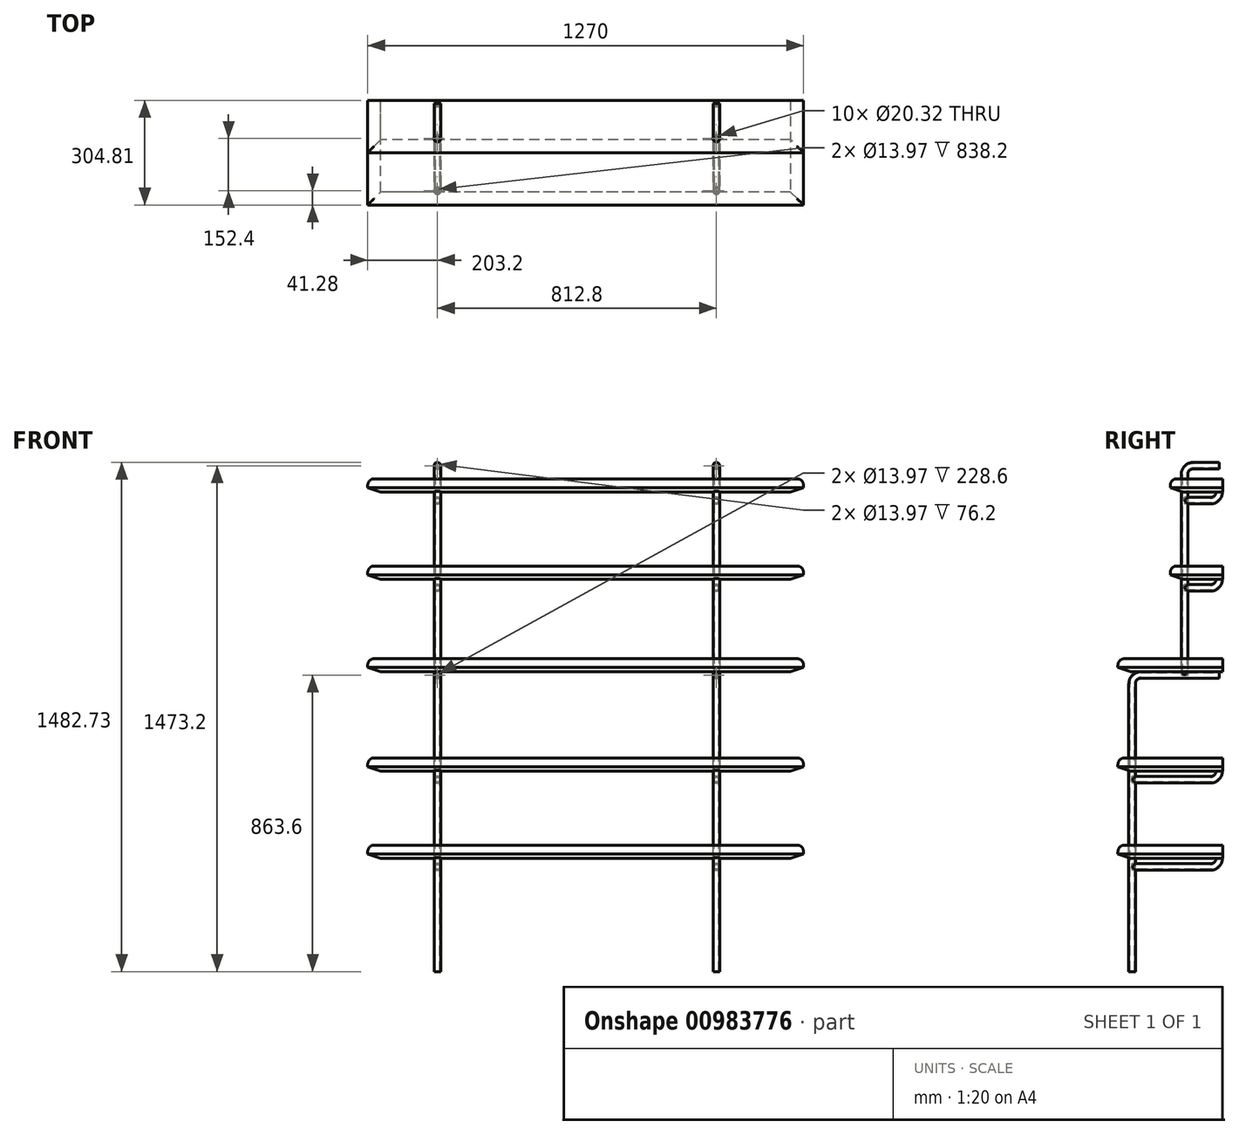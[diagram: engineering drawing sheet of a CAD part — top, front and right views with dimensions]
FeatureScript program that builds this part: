
annotation { "Feature Type Name" : "Feature", "Feature Type Description" : "" }
export const myFeature = defineFeature(function(context is Context, id is Id, definition is map)
    precondition{}
    {
        {
            assignVariable(context, id + "F0", {"name" : "SupportSeparation", "anyValue" : 32});
        }
        {
            var Q0;
            Q0=qCreatedBy(makeId("Right.planeOp"),FACE);
            cPlane(context, id + "F1", {"entities" : qUnion([Q0]), "cplaneType" : CPlaneType.OFFSET, "offset" : (getVariable(context, 'SupportSeparation') / 2) * mm, "width" : 152.4 * mm, "height" : 152.4 * mm});
        }
        {
            var Q0;
            Q0=qCreatedBy(makeId("Top.planeOp"),FACE);
            cPlane(context, id + "F2", {"entities" : qUnion([Q0]), "cplaneType" : CPlaneType.OFFSET, "offset" : 76.2 * mm, "oppositeDirection" : true, "width" : 152.4 * mm, "height" : 152.4 * mm});
        }
        {
            var Q0;
            Q0=qCreatedBy(id+"F1.planeOp",FACE);
            var sketch = newSketch(context, id + "F3", { "sketchPlane" : qUnion([Q0])});
            skLineSegment(sketch, "E0", {"start": v(-127, 0) * mm, "end": v(101.6, 0) * mm});
            skLineSegment(sketch, "E1", {"start": v(0, 0) * mm, "end": v(0, 584.2) * mm});
            skLineSegment(sketch, "E2", {"start": v(25.4, 609.6) * mm, "end": v(101.6, 609.6) * mm});
            skLineSegment(sketch, "E3", {"start": v(-152.4, -25.4) * mm, "end": v(-152.4, -863.6) * mm});
            skLineSegment(sketch, "E4", {"start": v(-152.4, -304.8) * mm, "end": v(76.2, -304.8) * mm});
            skLineSegment(sketch, "E5", {"start": v(-152.4, -558.8) * mm, "end": v(76.2, -558.8) * mm});
            skLineSegment(sketch, "E6", {"start": v(0, 508) * mm, "end": v(76.2, 508) * mm});
            skLineSegment(sketch, "E7", {"start": v(0, 254) * mm, "end": v(76.2, 254) * mm});
            skPoint(sketch, "E8.visualSharp", {"position": v(-152.4, 0) * mm});
            skArc(sketch, "E8.filletArc", {"start": v(-127, 0) * mm, "mid": v(-144.96, -7.44) * mm, "end": v(-152.4, -25.4) * mm});
            skPoint(sketch, "E9.visualSharp", {"position": v(0, 609.6) * mm});
            skArc(sketch, "E9.filletArc", {"start": v(25.4, 609.6) * mm, "mid": v(7.44, 602.16) * mm, "end": v(0, 584.2) * mm});
            skPoint(sketch, "E10.visualSharp", {"position": v(101.6, 508) * mm});
            skArc(sketch, "E10.filletArc", {"start": v(76.2, 508) * mm, "mid": v(94.16, 515.44) * mm, "end": v(101.6, 533.4) * mm});
            skPoint(sketch, "E11.visualSharp", {"position": v(101.6, 254) * mm});
            skArc(sketch, "E11.filletArc", {"start": v(76.2, 254) * mm, "mid": v(94.16, 261.44) * mm, "end": v(101.6, 279.4) * mm});
            skPoint(sketch, "E12.visualSharp", {"position": v(101.6, -304.8) * mm});
            skArc(sketch, "E12.filletArc", {"start": v(76.2, -304.8) * mm, "mid": v(94.16, -297.36) * mm, "end": v(101.6, -279.4) * mm});
            skPoint(sketch, "E13.visualSharp", {"position": v(101.6, -558.8) * mm});
            skArc(sketch, "E13.filletArc", {"start": v(76.2, -558.8) * mm, "mid": v(94.16, -551.36) * mm, "end": v(101.6, -533.4) * mm});
            skSolve(sketch);
        }
        {
            var Q0;
            Q0=qCreatedBy(id+"F2.planeOp",FACE);
            var sketch = newSketch(context, id + "F4", { "sketchPlane" : qUnion([Q0])});
            skCircle(sketch, "E14", {"center": v(406.4, -152.4) * mm, "radius": 9.52 * mm});
            skCircle(sketch, "E15", {"center": v(406.4, -152.4) * mm, "radius": 6.99 * mm});
            skSolve(sketch);
        }
        {
            var Q0;
            Q0=makeQuery(id+"F4.imprint","IMPRINT",FACE,{"disambiguationData":[TD([[makeQuery(id+"F4.imprint","IMPRINT",EDGE,{"derivedFrom":sQuery(id+"F4.wireOp",EDGE,"E14")}),1.0]])]});
            var Q1;
            Q1=sQuery(id+"F3.wireOp",EDGE,"E3");
            var Q2;
            Q2=sQuery(id+"F3.wireOp",EDGE,"E8.filletArc");
            var Q3;
            Q3=sQuery(id+"F3.wireOp",EDGE,"E0");
            sweep(context, id + "F5", {"profiles" : qUnion([Q0]), "path" : qUnion([Q1, Q2, Q3])});
        }
        {
            var Q0;
            Q0=qCreatedBy(makeId("Front.planeOp"),FACE);
            cPlane(context, id + "F6", {"entities" : qUnion([Q0]), "cplaneType" : CPlaneType.OFFSET, "offset" : 50.8 * mm, "oppositeDirection" : true, "width" : 152.4 * mm, "height" : 152.4 * mm});
        }
        {
            var Q0;
            Q0=qCreatedBy(id+"F6.planeOp",FACE);
            var sketch = newSketch(context, id + "F7", { "sketchPlane" : qUnion([Q0])});
            skCircle(sketch, "E16", {"center": v(406.4, -558.8) * mm, "radius": 9.53 * mm});
            skCircle(sketch, "E17", {"center": v(406.4, -558.8) * mm, "radius": 6.99 * mm});
            skCircle(sketch, "E18", {"center": v(406.4, -304.8) * mm, "radius": 9.53 * mm});
            skCircle(sketch, "E19", {"center": v(406.4, -304.8) * mm, "radius": 6.99 * mm});
            skCircle(sketch, "E20", {"center": v(406.4, 254) * mm, "radius": 6.99 * mm});
            skCircle(sketch, "E21", {"center": v(406.4, 254) * mm, "radius": 9.53 * mm});
            skCircle(sketch, "E22", {"center": v(406.4, 508) * mm, "radius": 6.99 * mm});
            skCircle(sketch, "E23", {"center": v(406.4, 508) * mm, "radius": 9.53 * mm});
            skCircle(sketch, "E24", {"center": v(406.4, 609.6) * mm, "radius": 6.99 * mm});
            skCircle(sketch, "E25", {"center": v(406.4, 609.6) * mm, "radius": 9.53 * mm});
            skSolve(sketch);
        }
        {
            var Q0;
            Q0=makeQuery(id+"F7.imprint","IMPRINT",FACE,{"disambiguationData":[TD([[makeQuery(id+"F7.imprint","IMPRINT",EDGE,{"derivedFrom":sQuery(id+"F7.wireOp",EDGE,"E24")}),-1.0]])]});
            var Q1;
            Q1=sQuery(id+"F3.wireOp",EDGE,"E2");
            var Q2;
            Q2=sQuery(id+"F3.wireOp",EDGE,"E9.filletArc");
            var Q3;
            Q3=sQuery(id+"F3.wireOp",EDGE,"E1");
            sweep(context, id + "F8", {"operationType" : NewBodyOperationType.ADD, "profiles" : qUnion([Q0]), "path" : qUnion([Q1, Q2, Q3])});
        }
        {
            var Q0;
            Q0=makeQuery(id+"F7.imprint","IMPRINT",FACE,{"disambiguationData":[TD([[makeQuery(id+"F7.imprint","IMPRINT",EDGE,{"derivedFrom":sQuery(id+"F7.wireOp",EDGE,"E22")}),-1.0]])]});
            var Q1;
            Q1=sQuery(id+"F3.wireOp",EDGE,"E6");
            var Q2;
            Q2=sQuery(id+"F3.wireOp",EDGE,"E10.filletArc");
            sweep(context, id + "F9", {"operationType" : NewBodyOperationType.ADD, "profiles" : qUnion([Q0]), "path" : qUnion([Q1, Q2])});
        }
        {
            var Q0;
            Q0=makeQuery(id+"F7.imprint","IMPRINT",FACE,{"disambiguationData":[TD([[makeQuery(id+"F7.imprint","IMPRINT",EDGE,{"derivedFrom":sQuery(id+"F7.wireOp",EDGE,"E20")}),-1.0]])]});
            var Q1;
            Q1=sQuery(id+"F3.wireOp",EDGE,"E7");
            var Q2;
            Q2=sQuery(id+"F3.wireOp",EDGE,"E11.filletArc");
            sweep(context, id + "F10", {"operationType" : NewBodyOperationType.ADD, "profiles" : qUnion([Q0]), "path" : qUnion([Q1, Q2])});
        }
        {
            var Q0;
            Q0=makeQuery(id+"F7.imprint","IMPRINT",FACE,{"disambiguationData":[TD([[makeQuery(id+"F7.imprint","IMPRINT",EDGE,{"derivedFrom":sQuery(id+"F7.wireOp",EDGE,"E16")}),1.0]])]});
            var Q1;
            Q1=sQuery(id+"F3.wireOp",EDGE,"E5");
            var Q2;
            Q2=sQuery(id+"F3.wireOp",EDGE,"E13.filletArc");
            sweep(context, id + "F11", {"operationType" : NewBodyOperationType.ADD, "profiles" : qUnion([Q0]), "path" : qUnion([Q1, Q2])});
        }
        {
            var Q0;
            Q0=makeQuery(id+"F7.imprint","IMPRINT",FACE,{"disambiguationData":[TD([[makeQuery(id+"F7.imprint","IMPRINT",EDGE,{"derivedFrom":sQuery(id+"F7.wireOp",EDGE,"E18")}),1.0]])]});
            var Q1;
            Q1=sQuery(id+"F3.wireOp",EDGE,"E4");
            var Q2;
            Q2=sQuery(id+"F3.wireOp",EDGE,"E12.filletArc");
            sweep(context, id + "F12", {"operationType" : NewBodyOperationType.ADD, "profiles" : qUnion([Q0]), "path" : qUnion([Q1, Q2])});
        }
        {
            var Q0;
            Q0=makeQuery(id+"F5.opSweep","SWEPT_BODY",BODY,{"disambiguationData":[OSD([sQuery(id+"F3.wireOp",EDGE,"E0"),sQuery(id+"F4.wireOp",EDGE,"E14"),sQuery(id+"F4.wireOp",EDGE,"E15")])]});
            var Q1;
            Q1=qCreatedBy(makeId("Right.planeOp"),FACE);
            mirror(context, id + "F13", {"entities" : qUnion([Q0]), "mirrorPlane" : qUnion([Q1])});
        }
        {
            var Q0;
            Q0=makeQuery(id+"F11.opSweep","CAP_FACE",FACE,{"disambiguationData":[OSD([sQuery(id+"F3.wireOp",VERTEX,"E13.filletArc.end"),sQuery(id+"F7.wireOp",EDGE,"E16"),sQuery(id+"F7.wireOp",EDGE,"E17")])],"isStart":true});
            var sketch = newSketch(context, id + "F14", { "sketchPlane" : qUnion([Q0])});
            skLineSegment(sketch, "E26.bottom", {"start": v(-609.6, 111.13) * mm, "end": v(660.4, 111.13) * mm});
            skLineSegment(sketch, "E26.top", {"start": v(-609.6, -193.68) * mm, "end": v(660.4, -193.68) * mm});
            skLineSegment(sketch, "E26.left", {"start": v(-609.6, 111.13) * mm, "end": v(-609.6, -193.68) * mm});
            skLineSegment(sketch, "E26.right", {"start": v(660.4, 111.13) * mm, "end": v(660.4, -193.68) * mm});
            skCircle(sketch, "E27", {"center": v(406.4, -152.4) * mm, "radius": 10.16 * mm});
            skLineSegment(sketch, "E28", {"start": v(0, 245.2) * mm, "end": v(0, -436.46) * mm, "construction": true});
            skCircle(sketch, "E29.MirrorC", {"center": v(-406.4, -152.4) * mm, "radius": 10.16 * mm});
            skSolve(sketch);
        }
        {
            var Q0;
            Q0=makeQuery(id+"F14.imprint","IMPRINT",FACE,{"disambiguationData":[TD([[makeQuery(id+"F14.imprint","IMPRINT",EDGE,{"derivedFrom":sQuery(id+"F14.wireOp",EDGE,"E26.top")}),1.0]])]});
            var Q1;
            Q1=makeQuery(id+"F14.imprint","IMPRINT",FACE,{"disambiguationData":[TD([[makeQuery(id+"F14.imprint","IMPRINT",EDGE,{"derivedFrom":makeQuery(id+"F11.opSweep","CAP_EDGE",EDGE,{"disambiguationData":[OSD([sQuery(id+"F3.wireOp",VERTEX,"E13.filletArc.end"),sQuery(id+"F7.wireOp",EDGE,"E17")])],"isStart":true})}),-1.0]])]});
            var Q2;
            {var subQ0=sQuery(id+"F3.wireOp",VERTEX,"E13.filletArc.end");Q2=makeQuery(id+"F14.imprint","IMPRINT",FACE,{"disambiguationData":[TD([[makeQuery(id+"F14.imprint","IMPRINT",EDGE,{"derivedFrom":makeQuery(id+"F11.opSweep","CAP_EDGE",EDGE,{"disambiguationData":[OSD([subQ0,sQuery(id+"F7.wireOp",EDGE,"E16")])],"isStart":true})}),-1.0]])]});}
            extrude(context, id + "F15", {"entities" : qUnion([Q0, Q1, Q2]), "depth" : 38.1 * mm, "offsetDistance" : 25.4 * mm});
        }
        {
            var Q0;
            Q0=makeQuery(id+"F15.opExtrude","CAP_EDGE",EDGE,{"disambiguationData":[OSD([sQuery(id+"F14.wireOp",EDGE,"E26.top")])],"isStart":false});
            var Q1;
            Q1=makeQuery(id+"F15.opExtrude","CAP_EDGE",EDGE,{"disambiguationData":[OSD([sQuery(id+"F14.wireOp",EDGE,"E26.right")])],"isStart":false});
            var Q2;
            Q2=makeQuery(id+"F15.opExtrude","CAP_EDGE",EDGE,{"disambiguationData":[OSD([sQuery(id+"F14.wireOp",EDGE,"E26.left")])],"isStart":false});
            fillet(context, id + "F16", {"entities" : qUnion([Q0, Q1, Q2]), "radius" : 19.05 * mm, "tangentPropagation" : true, "allowEdgeOverflow" : false});
        }
        {
            var Q0;
            Q0=makeQuery(id+"F15.opExtrude","CAP_EDGE",EDGE,{"disambiguationData":[OSD([sQuery(id+"F14.wireOp",EDGE,"E26.right")])],"isStart":true});
            var Q1;
            Q1=makeQuery(id+"F15.opExtrude","CAP_EDGE",EDGE,{"disambiguationData":[OSD([sQuery(id+"F14.wireOp",EDGE,"E26.top")])],"isStart":true});
            var Q2;
            Q2=makeQuery(id+"F15.opExtrude","CAP_EDGE",EDGE,{"disambiguationData":[OSD([sQuery(id+"F14.wireOp",EDGE,"E26.left")])],"isStart":true});
            chamfer(context, id + "F17", {"entities" : qUnion([Q0, Q1, Q2]), "chamferType" : ChamferType.TWO_OFFSETS, "width1" : 38.1 * mm, "oppositeDirection" : false, "width2" : 12.7 * mm, "tangentPropagation" : true});
        }
        {
            var Q0;
            Q0=qCreatedBy(id+"F1.planeOp",FACE);
            var sketch = newSketch(context, id + "F18", { "sketchPlane" : qUnion([Q0])});
            skLineSegment(sketch, "E30", {"start": v(101.6, -533.4) * mm, "end": v(101.6, -279.4) * mm});
            skSolve(sketch);
        }
        {
            var Q0;
            Q0=makeQuery(id+"F15.opExtrude","SWEPT_BODY",BODY,{"disambiguationData":[OSD([sQuery(id+"F14.wireOp",EDGE,"E26.bottom"),sQuery(id+"F14.wireOp",EDGE,"E26.top"),sQuery(id+"F14.wireOp",EDGE,"E26.left"),sQuery(id+"F14.wireOp",EDGE,"E26.right"),sQuery(id+"F14.wireOp",EDGE,"E27"),sQuery(id+"F14.wireOp",EDGE,"E29.MirrorC")])]});
            var Q1;
            Q1=sQuery(id+"F18.wireOp",EDGE,"E30");
            transform(context, id + "F19", {"entities" : qUnion([Q0]), "transformType" : TransformType.TRANSLATION_ENTITY, "oppositeDirectionEntity" : false, "transformLine" : qUnion([Q1]), "makeCopy" : true});
        }
        {
            var Q0;
            Q0=makeQuery(id+"F9.opSweep","CAP_FACE",FACE,{"disambiguationData":[OSD([sQuery(id+"F3.wireOp",VERTEX,"E10.filletArc.end"),sQuery(id+"F7.wireOp",EDGE,"E22"),sQuery(id+"F7.wireOp",EDGE,"E23")])],"isStart":true});
            var sketch = newSketch(context, id + "F20", { "sketchPlane" : qUnion([Q0])});
            skLineSegment(sketch, "E31.bottom", {"start": v(660.4, 111.13) * mm, "end": v(-609.6, 111.13) * mm});
            skLineSegment(sketch, "E31.top", {"start": v(660.4, -41.27) * mm, "end": v(-609.6, -41.27) * mm});
            skLineSegment(sketch, "E31.left", {"start": v(660.4, 111.13) * mm, "end": v(660.4, -41.27) * mm});
            skLineSegment(sketch, "E31.right", {"start": v(-609.6, 111.13) * mm, "end": v(-609.6, -41.27) * mm});
            skLineSegment(sketch, "E32", {"start": v(0, 162.2) * mm, "end": v(0, -203.72) * mm, "construction": true});
            skCircle(sketch, "E33", {"center": v(406.4, 0) * mm, "radius": 10.16 * mm});
            skCircle(sketch, "E34.MirrorC", {"center": v(-406.4, 0) * mm, "radius": 10.16 * mm});
            skSolve(sketch);
        }
        {
            var Q0;
            {var subQ0=sQuery(id+"F3.wireOp",VERTEX,"E10.filletArc.end");Q0=makeQuery(id+"F20.imprint","IMPRINT",FACE,{"disambiguationData":[TD([[makeQuery(id+"F20.imprint","IMPRINT",EDGE,{"derivedFrom":makeQuery(id+"F9.opSweep","CAP_EDGE",EDGE,{"disambiguationData":[OSD([subQ0,sQuery(id+"F7.wireOp",EDGE,"E22")])],"isStart":true})}),1.0]])]});}
            var Q1;
            Q1=makeQuery(id+"F20.imprint","IMPRINT",FACE,{"disambiguationData":[TD([[makeQuery(id+"F20.imprint","IMPRINT",EDGE,{"derivedFrom":sQuery(id+"F20.wireOp",EDGE,"E31.top")}),-1.0]])]});
            var Q2;
            Q2=makeQuery(id+"F20.imprint","IMPRINT",FACE,{"disambiguationData":[TD([[makeQuery(id+"F20.imprint","IMPRINT",EDGE,{"derivedFrom":makeQuery(id+"F9.opSweep","CAP_EDGE",EDGE,{"disambiguationData":[OSD([sQuery(id+"F3.wireOp",VERTEX,"E10.filletArc.end"),sQuery(id+"F7.wireOp",EDGE,"E22")])],"isStart":true})}),-1.0]])]});
            extrude(context, id + "F21", {"entities" : qUnion([Q0, Q1, Q2]), "depth" : 38.1 * mm, "offsetDistance" : 25.4 * mm});
        }
        {
            var Q0;
            Q0=makeQuery(id+"F21.opExtrude","CAP_EDGE",EDGE,{"disambiguationData":[OSD([sQuery(id+"F20.wireOp",EDGE,"E31.right")])],"isStart":false});
            var Q1;
            Q1=makeQuery(id+"F21.opExtrude","CAP_EDGE",EDGE,{"disambiguationData":[OSD([sQuery(id+"F20.wireOp",EDGE,"E31.top")])],"isStart":false});
            var Q2;
            Q2=makeQuery(id+"F21.opExtrude","CAP_EDGE",EDGE,{"disambiguationData":[OSD([sQuery(id+"F20.wireOp",EDGE,"E31.left")])],"isStart":false});
            fillet(context, id + "F22", {"entities" : qUnion([Q0, Q1, Q2]), "radius" : 19.05 * mm, "tangentPropagation" : true, "allowEdgeOverflow" : false});
        }
        {
            var Q0;
            Q0=makeQuery(id+"F21.opExtrude","CAP_EDGE",EDGE,{"disambiguationData":[OSD([sQuery(id+"F20.wireOp",EDGE,"E31.left")])],"isStart":true});
            var Q1;
            Q1=makeQuery(id+"F21.opExtrude","CAP_EDGE",EDGE,{"disambiguationData":[OSD([sQuery(id+"F20.wireOp",EDGE,"E31.top")])],"isStart":true});
            var Q2;
            Q2=makeQuery(id+"F21.opExtrude","CAP_EDGE",EDGE,{"disambiguationData":[OSD([sQuery(id+"F20.wireOp",EDGE,"E31.right")])],"isStart":true});
            chamfer(context, id + "F23", {"entities" : qUnion([Q0, Q1, Q2]), "chamferType" : ChamferType.TWO_OFFSETS, "width1" : 38.1 * mm, "oppositeDirection" : false, "width2" : 12.7 * mm, "tangentPropagation" : true});
        }
        {
            var Q0;
            Q0=qCreatedBy(id+"F1.planeOp",FACE);
            var sketch = newSketch(context, id + "F24", { "sketchPlane" : qUnion([Q0])});
            skLineSegment(sketch, "E35", {"start": v(101.6, 533.4) * mm, "end": v(101.6, 279.4) * mm});
            skSolve(sketch);
        }
        {
            var Q0;
            Q0=makeQuery(id+"F21.opExtrude","SWEPT_BODY",BODY,{"disambiguationData":[OSD([sQuery(id+"F20.wireOp",EDGE,"E31.bottom"),sQuery(id+"F20.wireOp",EDGE,"E31.top"),sQuery(id+"F20.wireOp",EDGE,"E31.left"),sQuery(id+"F20.wireOp",EDGE,"E31.right"),sQuery(id+"F20.wireOp",EDGE,"E33"),sQuery(id+"F20.wireOp",EDGE,"E34.MirrorC")])]});
            var Q1;
            Q1=sQuery(id+"F24.wireOp",EDGE,"E35");
            transform(context, id + "F25", {"entities" : qUnion([Q0]), "transformType" : TransformType.TRANSLATION_ENTITY, "oppositeDirectionEntity" : false, "transformLine" : qUnion([Q1]), "makeCopy" : true});
        }
        {
            var Q0;
            Q0=qCreatedBy(makeId("Top.planeOp"),FACE);
            cPlane(context, id + "F26", {"entities" : qUnion([Q0]), "cplaneType" : CPlaneType.OFFSET, "offset" : 9.52 * mm, "width" : 152.4 * mm, "height" : 152.4 * mm});
        }
        {
            var Q0;
            Q0=qCreatedBy(id+"F26.planeOp",FACE);
            var sketch = newSketch(context, id + "F27", { "sketchPlane" : qUnion([Q0])});
            skLineSegment(sketch, "E36.bottom", {"start": v(-609.6, 111.13) * mm, "end": v(660.4, 111.13) * mm});
            skLineSegment(sketch, "E36.top", {"start": v(-609.6, -193.67) * mm, "end": v(660.4, -193.67) * mm});
            skLineSegment(sketch, "E36.left", {"start": v(-609.6, 111.13) * mm, "end": v(-609.6, -193.67) * mm});
            skLineSegment(sketch, "E36.right", {"start": v(660.4, 111.13) * mm, "end": v(660.4, -193.67) * mm});
            skCircle(sketch, "E37", {"center": v(406.4, 0) * mm, "radius": 10.16 * mm});
            skLineSegment(sketch, "E38", {"start": v(0, 235.3) * mm, "end": v(0, -273) * mm, "construction": true});
            skCircle(sketch, "E39.MirrorC", {"center": v(-406.4, 0) * mm, "radius": 10.16 * mm});
            skSolve(sketch);
        }
        {
            var Q0;
            Q0=makeQuery(id+"F27.imprint","IMPRINT",FACE,{"disambiguationData":[TD([[makeQuery(id+"F27.imprint","IMPRINT",EDGE,{"derivedFrom":sQuery(id+"F27.wireOp",EDGE,"E36.bottom")}),-1.0]])]});
            extrude(context, id + "F28", {"entities" : qUnion([Q0]), "depth" : 38.1 * mm, "offsetDistance" : 25.4 * mm});
        }
        {
            var Q0;
            Q0=makeQuery(id+"F28.opExtrude","CAP_EDGE",EDGE,{"disambiguationData":[OSD([sQuery(id+"F27.wireOp",EDGE,"E36.left")])],"isStart":false});
            var Q1;
            Q1=makeQuery(id+"F28.opExtrude","CAP_EDGE",EDGE,{"disambiguationData":[OSD([sQuery(id+"F27.wireOp",EDGE,"E36.top")])],"isStart":false});
            var Q2;
            Q2=makeQuery(id+"F28.opExtrude","CAP_EDGE",EDGE,{"disambiguationData":[OSD([sQuery(id+"F27.wireOp",EDGE,"E36.right")])],"isStart":false});
            fillet(context, id + "F29", {"entities" : qUnion([Q0, Q1, Q2]), "radius" : 19.05 * mm, "tangentPropagation" : true, "allowEdgeOverflow" : false});
        }
        {
            var Q0;
            Q0=makeQuery(id+"F28.opExtrude","CAP_EDGE",EDGE,{"disambiguationData":[OSD([sQuery(id+"F27.wireOp",EDGE,"E36.right")])],"isStart":true});
            var Q1;
            Q1=makeQuery(id+"F28.opExtrude","CAP_EDGE",EDGE,{"disambiguationData":[OSD([sQuery(id+"F27.wireOp",EDGE,"E36.top")])],"isStart":true});
            var Q2;
            Q2=makeQuery(id+"F28.opExtrude","CAP_EDGE",EDGE,{"disambiguationData":[OSD([sQuery(id+"F27.wireOp",EDGE,"E36.left")])],"isStart":true});
            chamfer(context, id + "F30", {"entities" : qUnion([Q0, Q1, Q2]), "chamferType" : ChamferType.TWO_OFFSETS, "width1" : 38.1 * mm, "oppositeDirection" : false, "width2" : 12.7 * mm, "tangentPropagation" : true});
        }
    });
